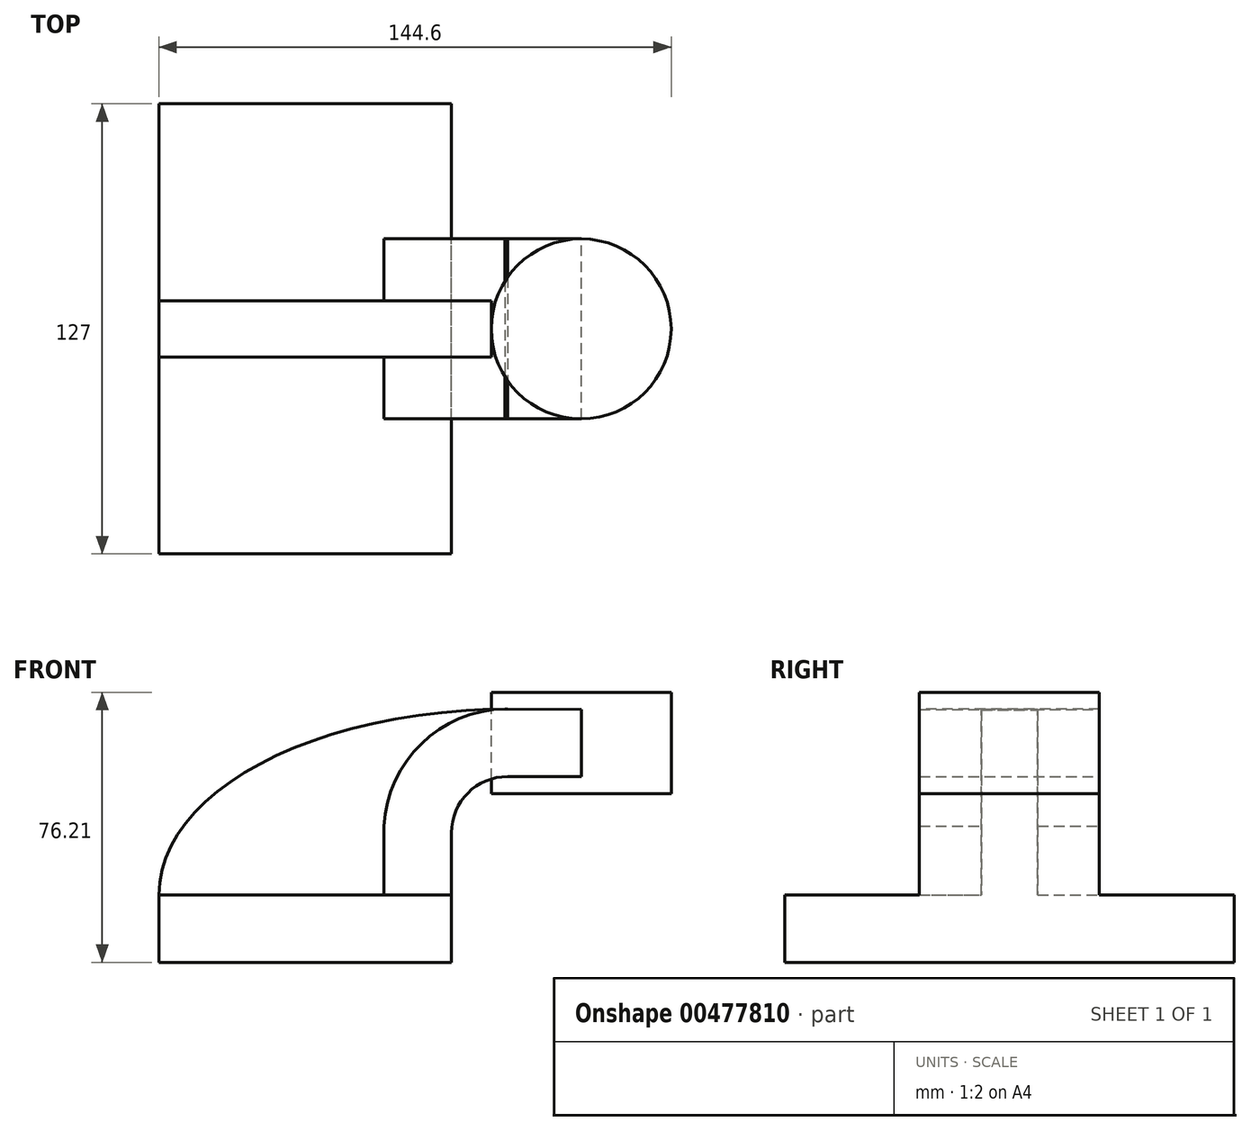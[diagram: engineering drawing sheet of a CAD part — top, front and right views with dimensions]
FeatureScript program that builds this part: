
annotation { "Feature Type Name" : "Feature", "Feature Type Description" : "" }
export const myFeature = defineFeature(function(context is Context, id is Id, definition is map)
    precondition{}
    {
        {
            var Q0;
            Q0=qCreatedBy(makeId("Front.planeOp"),FACE);
            var sketch = newSketch(context, id + "F0", { "sketchPlane" : qUnion([Q0])});
            skLineSegment(sketch, "E0.bottom", {"start": v(41.27, 9.53) * mm, "end": v(-41.28, 9.53) * mm});
            skLineSegment(sketch, "E0.top", {"start": v(41.28, -9.52) * mm, "end": v(-41.27, -9.52) * mm});
            skLineSegment(sketch, "E0.left", {"start": v(41.28, 9.53) * mm, "end": v(41.28, -9.52) * mm});
            skLineSegment(sketch, "E0.right", {"start": v(-41.28, 9.53) * mm, "end": v(-41.27, -9.52) * mm});
            skPoint(sketch, "E0.middle", {"position": v(0, 0) * mm});
            skLineSegment(sketch, "E1", {"start": v(41.27, 9.53) * mm, "end": v(41.27, 27) * mm});
            skArc(sketch, "E2", {"start": v(41.27, 27) * mm, "mid": v(45.92, 38.23) * mm, "end": v(57.15, 42.88) * mm});
            skLineSegment(sketch, "E3", {"start": v(57.15, 42.88) * mm, "end": v(77.92, 42.88) * mm});
            skArc(sketch, "E4.0", {"start": v(22.23, 28.9) * mm, "mid": v(33.1, 52.4) * mm, "end": v(57.15, 61.98) * mm});
            skLineSegment(sketch, "E5", {"start": v(22.22, 28.9) * mm, "end": v(22.22, 9.53) * mm});
            skLineSegment(sketch, "E6", {"start": v(57.15, 61.98) * mm, "end": v(77.92, 61.84) * mm});
            skLineSegment(sketch, "E7.bottom", {"start": v(103.32, 38.1) * mm, "end": v(52.52, 38.1) * mm});
            skLineSegment(sketch, "E7.top", {"start": v(103.32, 66.68) * mm, "end": v(52.52, 66.68) * mm});
            skLineSegment(sketch, "E7.left", {"start": v(103.32, 38.1) * mm, "end": v(103.32, 66.68) * mm});
            skLineSegment(sketch, "E7.right", {"start": v(52.52, 38.1) * mm, "end": v(52.52, 66.68) * mm});
            skPoint(sketch, "E7.middle", {"position": v(77.92, 52.39) * mm});
            skFitSpline(sketch, "E8", {"points": [v(-41.28, 9.53) * mm, v(57.15, 61.98) * mm], "startDerivative": vector(-0.43, 83.83) * mm, "endDerivative": vector(171.45, 1.49) * mm});
            skLineSegment(sketch, "E9", {"start": v(77.92, 66.68) * mm, "end": v(77.92, 38.1) * mm});
            skSolve(sketch);
        }
        {
            var Q0;
            Q0=makeQuery(id+"F0.imprint","IMPRINT",FACE,{"disambiguationData":[TD([[makeQuery(id+"F0.imprint","IMPRINT",EDGE,{"derivedFrom":sQuery(id+"F0.wireOp",EDGE,"E0.top")}),-1.0]])]});
            extrude(context, id + "F1", {"entities" : qUnion([Q0]), "endBound" : BoundingType.SYMMETRIC, "depth" : 127 * mm});
        }
        {
            var Q0;
            {var subQ0=sQuery(id+"F0.wireOp",EDGE,"E5");Q0=makeQuery(id+"F0.imprint","IMPRINT",FACE,{"disambiguationData":[TD([[makeQuery(id+"F0.imprint","IMPRINT",EDGE,{"derivedFrom":subQ0}),-1.0]])]});}
            extrude(context, id + "F2", {"entities" : qUnion([Q0]), "operationType" : NewBodyOperationType.ADD, "endBound" : BoundingType.SYMMETRIC, "depth" : 15.88 * mm});
        }
        {
            var Q0;
            {var subQ6=sQuery(id+"F0.wireOp",EDGE,"E1");Q0=makeQuery(id+"F0.imprint","IMPRINT",FACE,{"disambiguationData":[TD([[makeQuery(id+"F0.imprint","IMPRINT",EDGE,{"derivedFrom":subQ6}),1.0]])]});}
            var Q1;
            {var subQ6=sQuery(id+"F0.wireOp",EDGE,"E3");Q1=makeQuery(id+"F0.imprint","IMPRINT",FACE,{"disambiguationData":[TD([[makeQuery(id+"F0.imprint","IMPRINT",EDGE,{"derivedFrom":subQ6}),1.0]])]});}
            extrude(context, id + "F3", {"entities" : qUnion([Q0, Q1]), "operationType" : NewBodyOperationType.ADD, "endBound" : BoundingType.SYMMETRIC, "depth" : 50.8 * mm});
        }
        {
            var Q0;
            {var subQ0=sQuery(id+"F0.wireOp",EDGE,"E7.left");Q0=makeQuery(id+"F0.imprint","IMPRINT",FACE,{"disambiguationData":[TD([[makeQuery(id+"F0.imprint","IMPRINT",EDGE,{"derivedFrom":subQ0}),1.0]])]});}
            var Q1;
            Q1=sQuery(id+"F0.wireOp",EDGE,"E9");
            revolve(context, id + "F4", {"entities" : qUnion([Q0]), "axis" : qUnion([Q1]), "revolveType" : RevolveType.FULL});
        }
    });
